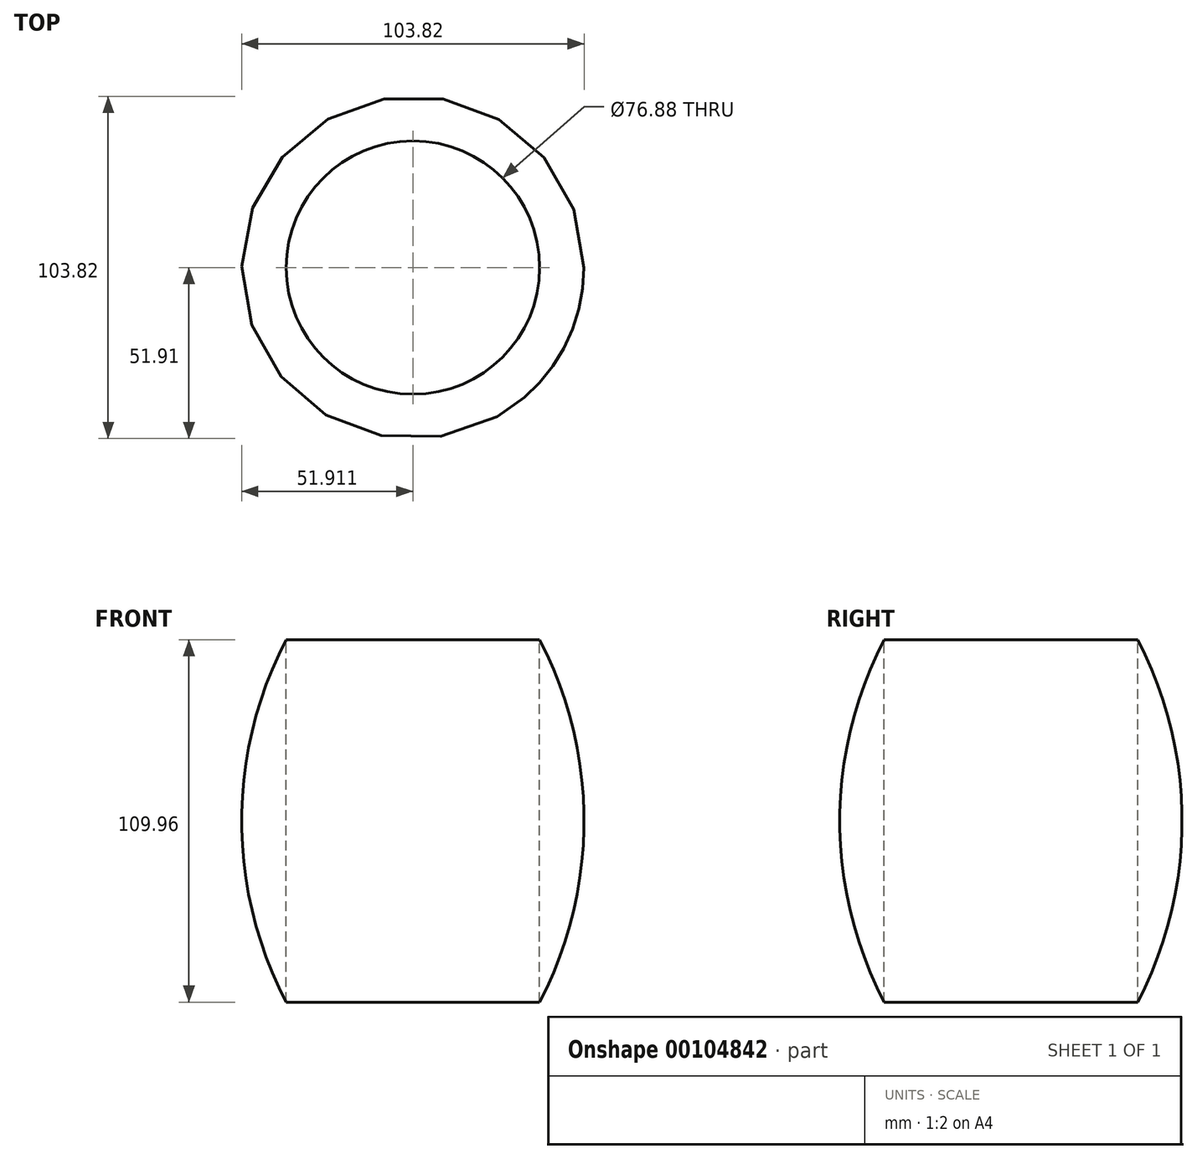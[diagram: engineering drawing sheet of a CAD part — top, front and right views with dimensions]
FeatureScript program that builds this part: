
annotation { "Feature Type Name" : "Feature", "Feature Type Description" : "" }
export const myFeature = defineFeature(function(context is Context, id is Id, definition is map)
    precondition{}
    {
        {
            var Q0;
            Q0=qCreatedBy(makeId("Front.planeOp"),FACE);
            var sketch = newSketch(context, id + "F0", { "sketchPlane" : qUnion([Q0])});
            skLineSegment(sketch, "E0", {"start": v(-14.9, 60.94) * mm, "end": v(-14.9, -48.72) * mm});
            skLineSegment(sketch, "E1", {"start": v(-53.34, 60.94) * mm, "end": v(-53.34, -49.02) * mm});
            skArc(sketch, "E2", {"start": v(-53.34, 60.94) * mm, "mid": v(-66.8, 5.96) * mm, "end": v(-53.34, -49.02) * mm});
            skSolve(sketch);
        }
        {
            var Q0;
            Q0 = qSketchRegion(id + "F0", true);
            var Q1;
            Q1=sQuery(id+"F0.wireOp",EDGE,"E0");
            revolve(context, id + "F1", {"entities" : qUnion([Q0]), "axis" : qUnion([Q1]), "revolveType" : RevolveType.FULL});
        }
    });
